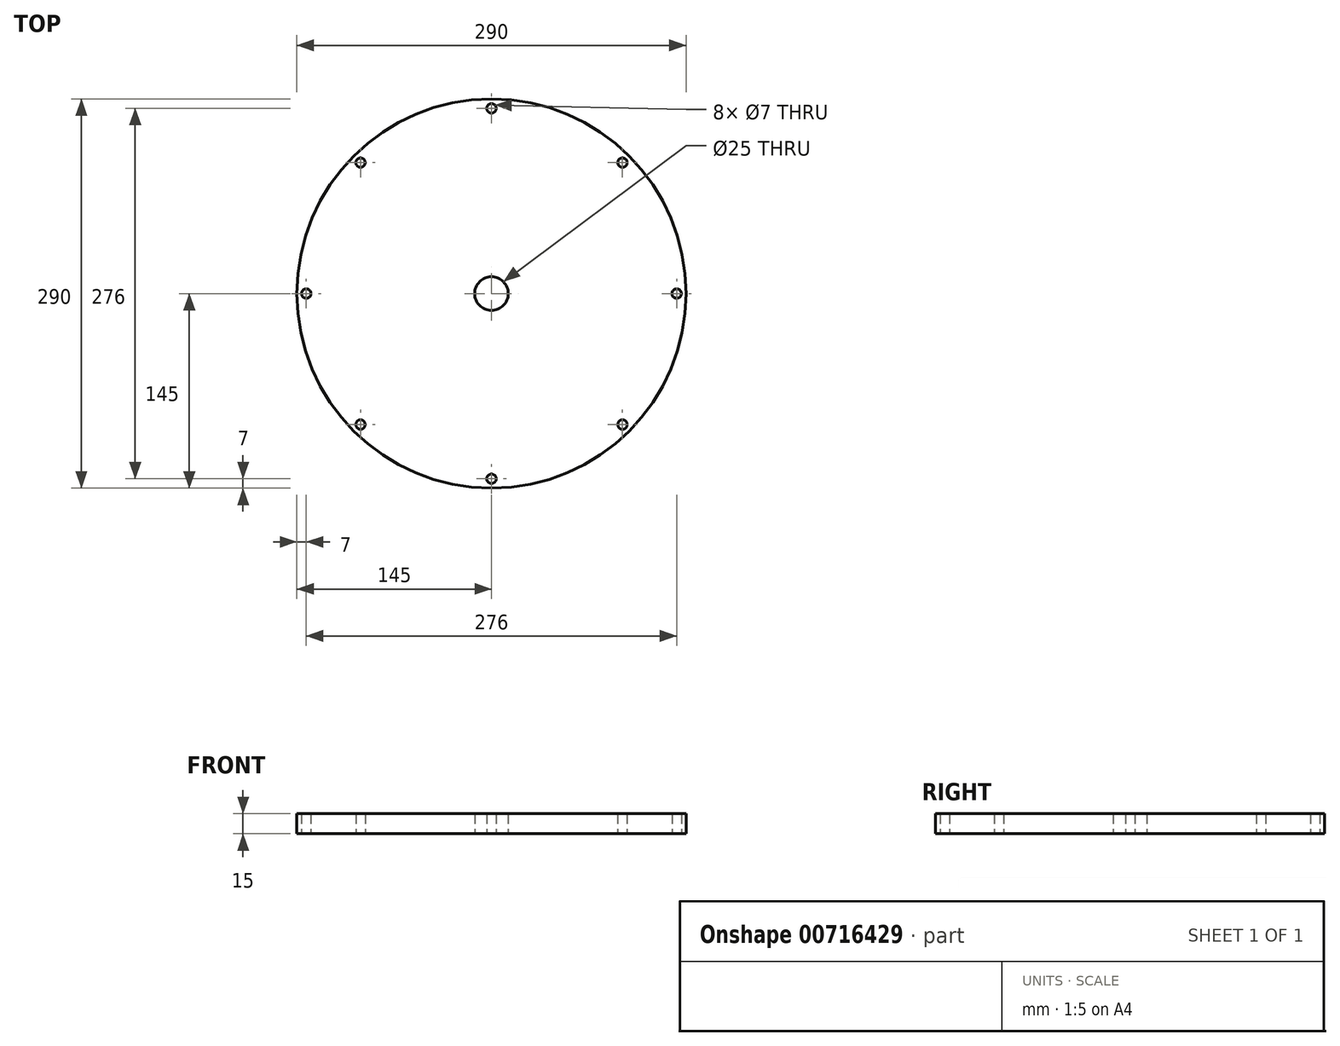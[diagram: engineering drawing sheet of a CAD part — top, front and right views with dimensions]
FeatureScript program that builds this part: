
annotation { "Feature Type Name" : "Feature", "Feature Type Description" : "" }
export const myFeature = defineFeature(function(context is Context, id is Id, definition is map)
    precondition{}
    {
        {
            var Q0;
            Q0=qCreatedBy(makeId("Top.planeOp"),FACE);
            var sketch = newSketch(context, id + "F0", { "sketchPlane" : qUnion([Q0])});
            skCircle(sketch, "E0", {"center": v(0, 0) * mm, "radius": 145 * mm});
            skCircle(sketch, "E1", {"center": v(0, 138) * mm, "radius": 3.5 * mm});
            skCircle(sketch, "E2.1.0", {"center": v(-97.58, 97.58) * mm, "radius": 3.5 * mm});
            skCircle(sketch, "E2.2.0", {"center": v(-138, 0) * mm, "radius": 3.5 * mm});
            skCircle(sketch, "E2.3.0", {"center": v(-97.58, -97.58) * mm, "radius": 3.5 * mm});
            skCircle(sketch, "E2.4.0", {"center": v(0, -138) * mm, "radius": 3.5 * mm});
            skCircle(sketch, "E2.5.0", {"center": v(97.58, -97.58) * mm, "radius": 3.5 * mm});
            skCircle(sketch, "E2.6.0", {"center": v(138, 0) * mm, "radius": 3.5 * mm});
            skCircle(sketch, "E2.7.0", {"center": v(97.58, 97.58) * mm, "radius": 3.5 * mm});
            skCircle(sketch, "E3", {"center": v(0, 0) * mm, "radius": 12.5 * mm});
            skSolve(sketch);
        }
        {
            var Q0;
            Q0 = qSketchRegion(id + "F0", true);
            extrude(context, id + "F1", {"entities" : qUnion([Q0]), "depth" : 15 * mm, "offsetDistance" : 25 * mm});
        }
    });
